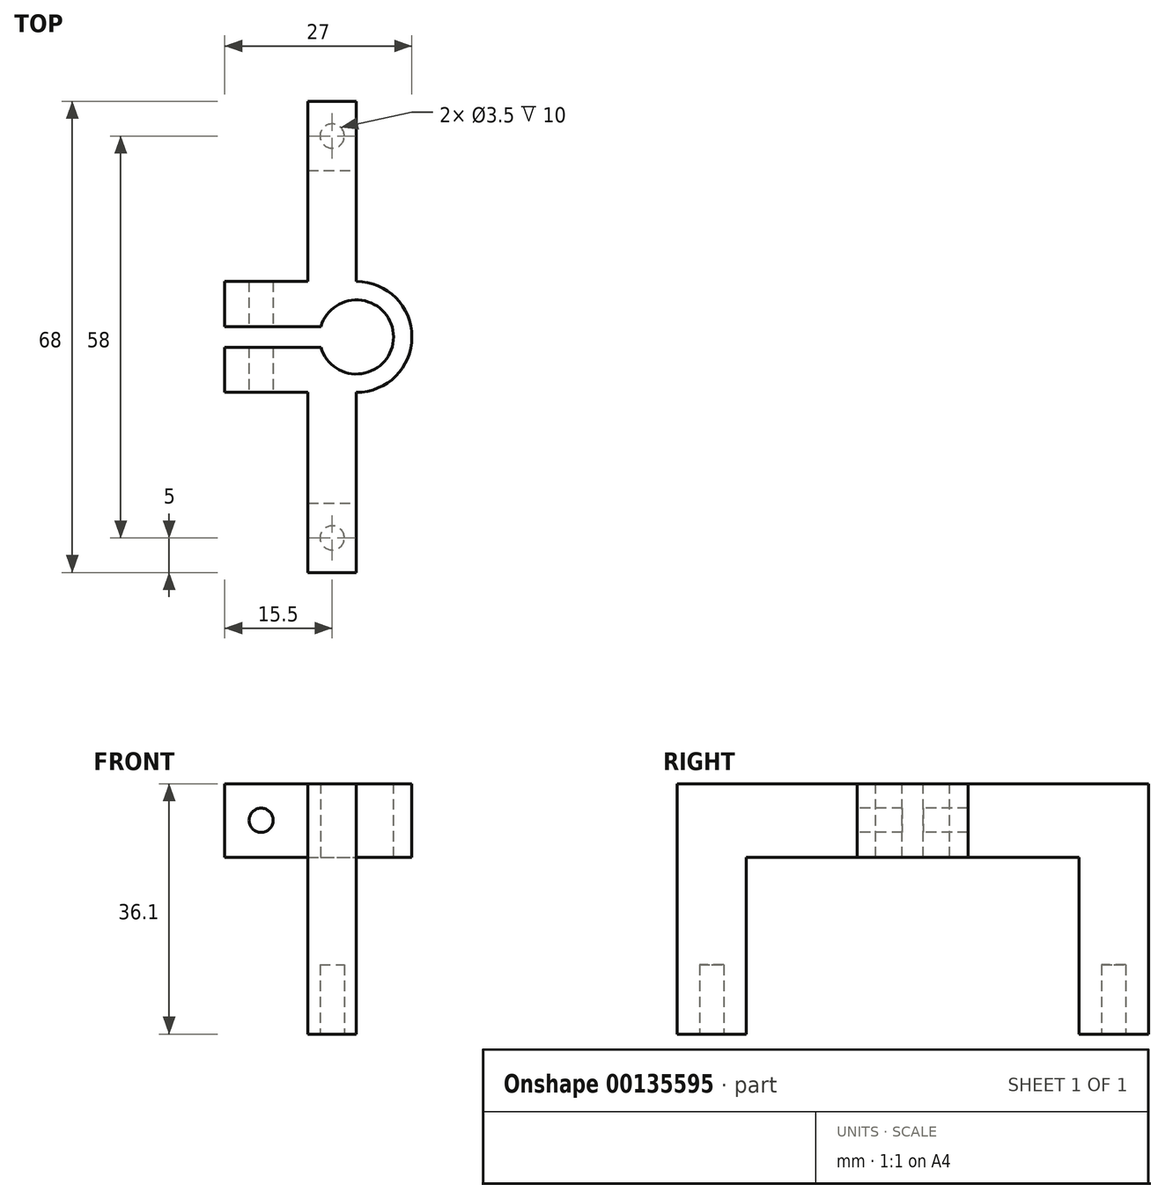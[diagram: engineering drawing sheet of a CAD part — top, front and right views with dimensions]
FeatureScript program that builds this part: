
annotation { "Feature Type Name" : "Feature", "Feature Type Description" : "" }
export const myFeature = defineFeature(function(context is Context, id is Id, definition is map)
    precondition{}
    {
        {
            var Q0;
            Q0=qCreatedBy(makeId("Top.planeOp"),FACE);
            var sketch = newSketch(context, id + "F0", { "sketchPlane" : qUnion([Q0])});
            skCircle(sketch, "E0", {"center": v(0, 0) * mm, "radius": 8 * mm});
            skSolve(sketch);
        }
        {
            var Q0;
            Q0 = qSketchRegion(id + "F0", true);
            extrude(context, id + "F1", {"entities" : qUnion([Q0]), "oppositeDirection" : true, "depth" : 10.6 * mm});
        }
        {
            var Q0;
            Q0=makeQuery(id+"F1.opExtrude","CAP_FACE",FACE,{"disambiguationData":[OSD([sQuery(id+"F0.wireOp",EDGE,"E0")])],"isStart":true});
            var sketch = newSketch(context, id + "F2", { "sketchPlane" : qUnion([Q0])});
            skLineSegment(sketch, "E1.bottom", {"start": v(0, 8) * mm, "end": v(-19, 8) * mm});
            skLineSegment(sketch, "E1.top", {"start": v(0, 1.5) * mm, "end": v(-19, 1.5) * mm});
            skLineSegment(sketch, "E1.left", {"start": v(0, 8) * mm, "end": v(0, 1.5) * mm});
            skLineSegment(sketch, "E1.right", {"start": v(-19, 8) * mm, "end": v(-19, 1.5) * mm});
            skLineSegment(sketch, "E2.bottom", {"start": v(0, -8) * mm, "end": v(-19, -8) * mm});
            skLineSegment(sketch, "E2.top", {"start": v(0, -1.5) * mm, "end": v(-19, -1.5) * mm});
            skLineSegment(sketch, "E2.left", {"start": v(0, -8) * mm, "end": v(0, -1.5) * mm});
            skLineSegment(sketch, "E2.right", {"start": v(-19, -8) * mm, "end": v(-19, -1.5) * mm});
            skSolve(sketch);
        }
        {
            var Q0;
            Q0 = qSketchRegion(id + "F2", true);
            var Q1;
            Q1=makeQuery(id+"F1.opExtrude","CAP_FACE",FACE,{"disambiguationData":[OSD([sQuery(id+"F0.wireOp",EDGE,"E0")])],"isStart":false});
            extrude(context, id + "F3", {"entities" : qUnion([Q0]), "operationType" : NewBodyOperationType.ADD, "endBound" : BoundingType.UP_TO_SURFACE, "oppositeDirection" : true, "endBoundEntityFace" : qUnion([Q1]), "depth" : 25 * mm});
        }
        {
            var Q0;
            Q0=makeQuery(id+"F3.boolean.opBoolean","MERGE",FACE,{"derivedFrom":[makeQuery(id+"F1.opExtrude","CAP_FACE",FACE,{"disambiguationData":[OSD([sQuery(id+"F0.wireOp",EDGE,"E0")])],"isStart":true}),makeQuery(id+"F3.opExtrude","CAP_FACE",FACE,{"disambiguationData":[OSD([sQuery(id+"F2.wireOp",EDGE,"E1.bottom"),sQuery(id+"F2.wireOp",EDGE,"E1.top"),sQuery(id+"F2.wireOp",EDGE,"E1.left"),sQuery(id+"F2.wireOp",EDGE,"E1.right")])],"isStart":true}),makeQuery(id+"F3.opExtrude","CAP_FACE",FACE,{"disambiguationData":[OSD([sQuery(id+"F2.wireOp",EDGE,"E2.bottom"),sQuery(id+"F2.wireOp",EDGE,"E2.top"),sQuery(id+"F2.wireOp",EDGE,"E2.left"),sQuery(id+"F2.wireOp",EDGE,"E2.right")])],"isStart":true})]});
            var sketch = newSketch(context, id + "F4", { "sketchPlane" : qUnion([Q0])});
            skCircle(sketch, "E3", {"center": v(0, 0) * mm, "radius": 5.35 * mm});
            skSolve(sketch);
        }
        {
            var Q0;
            Q0 = qSketchRegion(id + "F4", true);
            extrude(context, id + "F5", {"entities" : qUnion([Q0]), "operationType" : NewBodyOperationType.REMOVE, "endBound" : BoundingType.THROUGH_ALL, "oppositeDirection" : true, "depth" : 25 * mm});
        }
        {
            var Q0;
            Q0=makeQuery(id+"F3.boolean.opBoolean","MERGE",FACE,{"derivedFrom":[makeQuery(id+"F1.opExtrude","CAP_FACE",FACE,{"disambiguationData":[OSD([sQuery(id+"F0.wireOp",EDGE,"E0")])],"isStart":true}),makeQuery(id+"F3.opExtrude","CAP_FACE",FACE,{"disambiguationData":[OSD([sQuery(id+"F2.wireOp",EDGE,"E1.bottom"),sQuery(id+"F2.wireOp",EDGE,"E1.top"),sQuery(id+"F2.wireOp",EDGE,"E1.left"),sQuery(id+"F2.wireOp",EDGE,"E1.right")])],"isStart":true}),makeQuery(id+"F3.opExtrude","CAP_FACE",FACE,{"disambiguationData":[OSD([sQuery(id+"F2.wireOp",EDGE,"E2.bottom"),sQuery(id+"F2.wireOp",EDGE,"E2.top"),sQuery(id+"F2.wireOp",EDGE,"E2.left"),sQuery(id+"F2.wireOp",EDGE,"E2.right")])],"isStart":true})]});
            var sketch = newSketch(context, id + "F6", { "sketchPlane" : qUnion([Q0])});
            skLineSegment(sketch, "E4.bottom", {"start": v(-5.14, -1.5) * mm, "end": v(-10.58, -1.5) * mm});
            skLineSegment(sketch, "E4.top", {"start": v(-5.14, 1.5) * mm, "end": v(-10.58, 1.5) * mm});
            skLineSegment(sketch, "E4.left", {"start": v(-5.14, -1.5) * mm, "end": v(-5.14, 1.5) * mm});
            skLineSegment(sketch, "E4.right", {"start": v(-10.58, -1.5) * mm, "end": v(-10.58, 1.5) * mm});
            skPoint(sketch, "E4.middle", {"position": v(-7.86, 0) * mm});
            skSolve(sketch);
        }
        {
            var Q0;
            Q0 = qSketchRegion(id + "F6", true);
            extrude(context, id + "F7", {"entities" : qUnion([Q0]), "operationType" : NewBodyOperationType.REMOVE, "endBound" : BoundingType.THROUGH_ALL, "oppositeDirection" : true, "depth" : 25 * mm});
        }
        {
            var Q0;
            Q0=makeQuery(id+"F3.opExtrude","SWEPT_FACE",FACE,{"disambiguationData":[OSD([sQuery(id+"F2.wireOp",EDGE,"E2.bottom")])]});
            var sketch = newSketch(context, id + "F8", { "sketchPlane" : qUnion([Q0])});
            skCircle(sketch, "E5", {"center": v(-13.75, -5.25) * mm, "radius": 1.75 * mm});
            skSolve(sketch);
        }
        {
            var Q0;
            Q0 = qSketchRegion(id + "F8", true);
            extrude(context, id + "F9", {"entities" : qUnion([Q0]), "operationType" : NewBodyOperationType.REMOVE, "endBound" : BoundingType.THROUGH_ALL, "oppositeDirection" : true, "depth" : 25 * mm});
        }
        {
            var Q0;
            Q0=makeQuery(id+"F3.opExtrude","SWEPT_FACE",FACE,{"disambiguationData":[OSD([sQuery(id+"F2.wireOp",EDGE,"E2.bottom")])]});
            var sketch = newSketch(context, id + "F10", { "sketchPlane" : qUnion([Q0])});
            skLineSegment(sketch, "E6.bottom", {"start": v(-7, 0) * mm, "end": v(0, 0) * mm});
            skLineSegment(sketch, "E6.top", {"start": v(-7, -10.6) * mm, "end": v(0, -10.6) * mm});
            skLineSegment(sketch, "E6.left", {"start": v(-7, 0) * mm, "end": v(-7, -10.6) * mm});
            skLineSegment(sketch, "E6.right", {"start": v(0, 0) * mm, "end": v(0, -10.6) * mm});
            skSolve(sketch);
        }
        {
            var Q0;
            Q0 = qSketchRegion(id + "F10", true);
            extrude(context, id + "F11", {"entities" : qUnion([Q0]), "operationType" : NewBodyOperationType.ADD, "depth" : 26 * mm});
        }
        {
            var Q0;
            {var subQ0=sQuery(id+"F0.wireOp",EDGE,"E0");Q0=makeQuery(id+"F11.boolean.opBoolean","MERGE",FACE,{"derivedFrom":[makeQuery(id+"F3.boolean.opBoolean","MERGE",FACE,{"derivedFrom":[makeQuery(id+"F1.opExtrude","CAP_FACE",FACE,{"disambiguationData":[OSD([subQ0])],"isStart":false}),makeQuery(id+"F3.opExtrude","CAP_FACE",FACE,{"disambiguationData":[OSD([subQ0]),ownerDisambiguation([makeQuery(id+"F3.opExtrude","SWEPT_BODY",BODY,{"disambiguationData":[OSD([sQuery(id+"F2.wireOp",EDGE,"E1.bottom"),sQuery(id+"F2.wireOp",EDGE,"E1.top"),sQuery(id+"F2.wireOp",EDGE,"E1.left"),sQuery(id+"F2.wireOp",EDGE,"E1.right")])]})])],"isStart":false}),makeQuery(id+"F3.opExtrude","CAP_FACE",FACE,{"disambiguationData":[OSD([subQ0]),ownerDisambiguation([makeQuery(id+"F3.opExtrude","SWEPT_BODY",BODY,{"disambiguationData":[OSD([sQuery(id+"F2.wireOp",EDGE,"E2.bottom"),sQuery(id+"F2.wireOp",EDGE,"E2.top"),sQuery(id+"F2.wireOp",EDGE,"E2.left"),sQuery(id+"F2.wireOp",EDGE,"E2.right")])]})])],"isStart":false})]}),makeQuery(id+"F11.opExtrude","SWEPT_FACE",FACE,{"disambiguationData":[OSD([sQuery(id+"F10.wireOp",EDGE,"E6.top")])]})]});}
            var sketch = newSketch(context, id + "F12", { "sketchPlane" : qUnion([Q0])});
            skLineSegment(sketch, "E7.bottom", {"start": v(-7, 34) * mm, "end": v(0, 34) * mm});
            skLineSegment(sketch, "E7.top", {"start": v(-7, 24) * mm, "end": v(0, 24) * mm});
            skLineSegment(sketch, "E7.left", {"start": v(-7, 34) * mm, "end": v(-7, 24) * mm});
            skLineSegment(sketch, "E7.right", {"start": v(0, 34) * mm, "end": v(0, 24) * mm});
            skSolve(sketch);
        }
        {
            var Q0;
            Q0 = qSketchRegion(id + "F12", true);
            extrude(context, id + "F13", {"entities" : qUnion([Q0]), "operationType" : NewBodyOperationType.ADD, "depth" : 25.5 * mm});
        }
        {
            var Q0;
            Q0=makeQuery(id+"F3.opExtrude","SWEPT_FACE",FACE,{"disambiguationData":[OSD([sQuery(id+"F2.wireOp",EDGE,"E1.bottom")])]});
            var sketch = newSketch(context, id + "F14", { "sketchPlane" : qUnion([Q0])});
            skLineSegment(sketch, "E8.bottom", {"start": v(0, 0) * mm, "end": v(7, 0) * mm});
            skLineSegment(sketch, "E8.top", {"start": v(0, -10.6) * mm, "end": v(7, -10.6) * mm});
            skLineSegment(sketch, "E8.left", {"start": v(0, 0) * mm, "end": v(0, -10.6) * mm});
            skLineSegment(sketch, "E8.right", {"start": v(7, 0) * mm, "end": v(7, -10.6) * mm});
            skSolve(sketch);
        }
        {
            var Q0;
            Q0 = qSketchRegion(id + "F14", true);
            extrude(context, id + "F15", {"entities" : qUnion([Q0]), "operationType" : NewBodyOperationType.ADD, "depth" : 26 * mm});
        }
        {
            var Q0;
            {var subQ0=sQuery(id+"F0.wireOp",EDGE,"E0");Q0=makeQuery(id+"F15.boolean.opBoolean","MERGE",FACE,{"derivedFrom":[makeQuery(id+"F11.boolean.opBoolean","MERGE",FACE,{"derivedFrom":[makeQuery(id+"F3.boolean.opBoolean","MERGE",FACE,{"derivedFrom":[makeQuery(id+"F1.opExtrude","CAP_FACE",FACE,{"disambiguationData":[OSD([subQ0])],"isStart":false}),makeQuery(id+"F3.opExtrude","CAP_FACE",FACE,{"disambiguationData":[OSD([subQ0]),ownerDisambiguation([makeQuery(id+"F3.opExtrude","SWEPT_BODY",BODY,{"disambiguationData":[OSD([sQuery(id+"F2.wireOp",EDGE,"E1.bottom"),sQuery(id+"F2.wireOp",EDGE,"E1.top"),sQuery(id+"F2.wireOp",EDGE,"E1.left"),sQuery(id+"F2.wireOp",EDGE,"E1.right")])]})])],"isStart":false}),makeQuery(id+"F3.opExtrude","CAP_FACE",FACE,{"disambiguationData":[OSD([subQ0]),ownerDisambiguation([makeQuery(id+"F3.opExtrude","SWEPT_BODY",BODY,{"disambiguationData":[OSD([sQuery(id+"F2.wireOp",EDGE,"E2.bottom"),sQuery(id+"F2.wireOp",EDGE,"E2.top"),sQuery(id+"F2.wireOp",EDGE,"E2.left"),sQuery(id+"F2.wireOp",EDGE,"E2.right")])]})])],"isStart":false})]}),makeQuery(id+"F11.opExtrude","SWEPT_FACE",FACE,{"disambiguationData":[OSD([sQuery(id+"F10.wireOp",EDGE,"E6.top")])]})]}),makeQuery(id+"F15.opExtrude","SWEPT_FACE",FACE,{"disambiguationData":[OSD([sQuery(id+"F14.wireOp",EDGE,"E8.top")])]})]});}
            var sketch = newSketch(context, id + "F16", { "sketchPlane" : qUnion([Q0])});
            skLineSegment(sketch, "E9.bottom", {"start": v(-7, -34) * mm, "end": v(0, -34) * mm});
            skLineSegment(sketch, "E9.top", {"start": v(-7, -24) * mm, "end": v(0, -24) * mm});
            skLineSegment(sketch, "E9.left", {"start": v(-7, -34) * mm, "end": v(-7, -24) * mm});
            skLineSegment(sketch, "E9.right", {"start": v(0, -34) * mm, "end": v(0, -24) * mm});
            skSolve(sketch);
        }
        {
            var Q0;
            Q0 = qSketchRegion(id + "F16", true);
            extrude(context, id + "F17", {"entities" : qUnion([Q0]), "operationType" : NewBodyOperationType.ADD, "depth" : 25.5 * mm});
        }
        {
            var Q0;
            Q0=makeQuery(id+"F13.opExtrude","CAP_FACE",FACE,{"disambiguationData":[OSD([sQuery(id+"F12.wireOp",EDGE,"E7.bottom"),sQuery(id+"F12.wireOp",EDGE,"E7.top"),sQuery(id+"F12.wireOp",EDGE,"E7.left"),sQuery(id+"F12.wireOp",EDGE,"E7.right")])],"isStart":false});
            var sketch = newSketch(context, id + "F18", { "sketchPlane" : qUnion([Q0])});
            skCircle(sketch, "E10", {"center": v(-3.5, 29) * mm, "radius": 1.75 * mm});
            skPoint(sketch, "E10.centerSnap0", {"position": v(-7, 29) * mm});
            skLineSegment(sketch, "E11", {"start": v(-3.5, 34) * mm, "end": v(-3.5, 24) * mm, "construction": true});
            skLineSegment(sketch, "E12", {"start": v(-3.5, -24) * mm, "end": v(-3.5, -34) * mm, "construction": true});
            skCircle(sketch, "E13", {"center": v(-3.5, -29) * mm, "radius": 1.75 * mm});
            skSolve(sketch);
        }
        {
            var Q0;
            Q0 = qSketchRegion(id + "F18", true);
            extrude(context, id + "F19", {"entities" : qUnion([Q0]), "operationType" : NewBodyOperationType.REMOVE, "oppositeDirection" : true, "depth" : 10 * mm});
        }
    });
